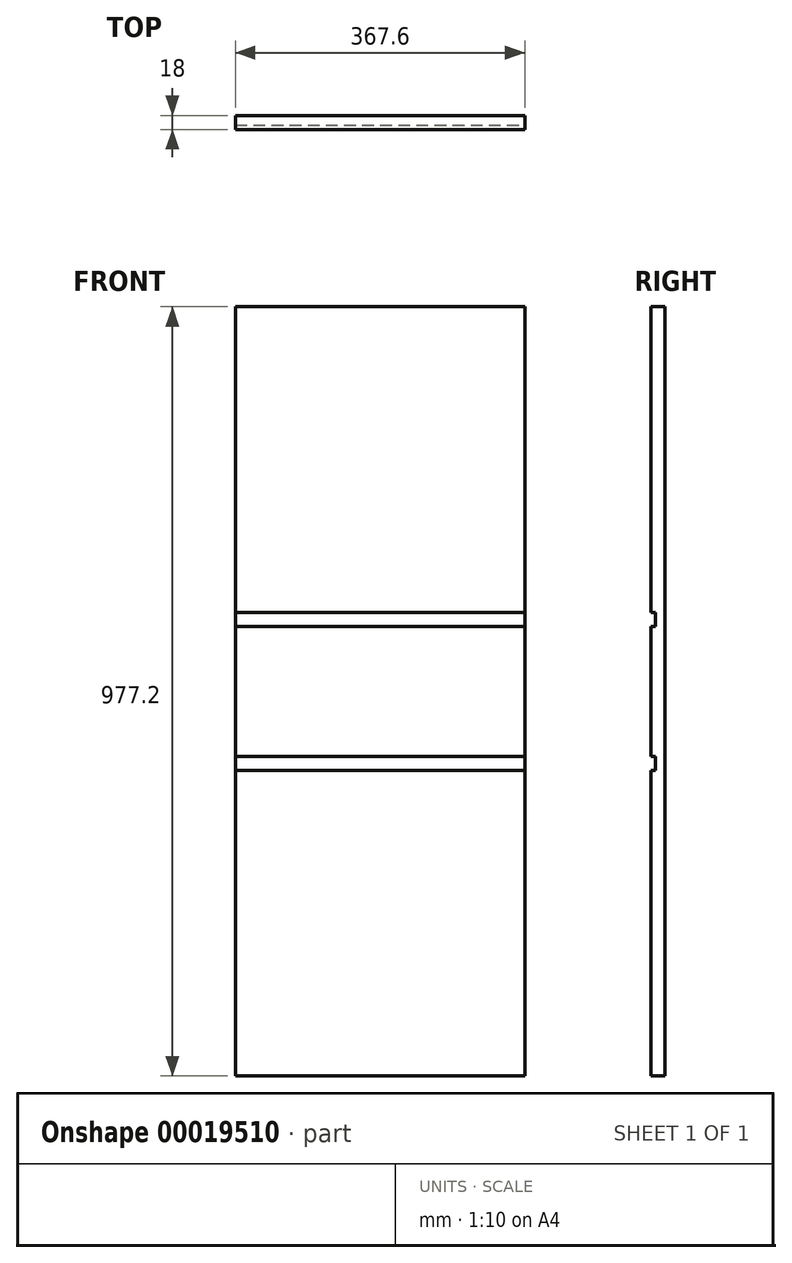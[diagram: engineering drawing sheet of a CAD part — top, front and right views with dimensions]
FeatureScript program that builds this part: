
annotation { "Feature Type Name" : "Feature", "Feature Type Description" : "" }
export const myFeature = defineFeature(function(context is Context, id is Id, definition is map)
    precondition{}
    {
        {
            var Q0;
            Q0=qCreatedBy(makeId("Front.planeOp"),FACE);
            var sketch = newSketch(context, id + "F0", { "sketchPlane" : qUnion([Q0])});
            skLineSegment(sketch, "E0.bottom", {"start": v(-210.04, 655.45) * mm, "end": v(157.56, 655.45) * mm});
            skLineSegment(sketch, "E0.top", {"start": v(-210.04, -321.75) * mm, "end": v(157.56, -321.75) * mm});
            skLineSegment(sketch, "E0.left", {"start": v(-210.04, 655.45) * mm, "end": v(-210.04, -321.75) * mm});
            skLineSegment(sketch, "E0.right", {"start": v(157.56, 655.45) * mm, "end": v(157.56, -321.75) * mm});
            skSolve(sketch);
        }
        {
            var Q0;
            Q0 = qSketchRegion(id + "F0", true);
            extrude(context, id + "F1", {"entities" : qUnion([Q0]), "depth" : 18 * mm});
        }
        {
            var Q0;
            Q0=makeQuery(id+"F1.opExtrude","CAP_FACE",FACE,{"disambiguationData":[OSD([sQuery(id+"F0.wireOp",EDGE,"E0.bottom"),sQuery(id+"F0.wireOp",EDGE,"E0.top"),sQuery(id+"F0.wireOp",EDGE,"E0.left"),sQuery(id+"F0.wireOp",EDGE,"E0.right")])],"isStart":false});
            var sketch = newSketch(context, id + "F2", { "sketchPlane" : qUnion([Q0])});
            skLineSegment(sketch, "E1", {"start": v(-210.04, 166.85) * mm, "end": v(157.56, 166.85) * mm, "construction": true});
            skLineSegment(sketch, "E2", {"start": v(-26.24, 655.45) * mm, "end": v(-26.24, -321.75) * mm, "construction": true});
            skLineSegment(sketch, "E3.bottom", {"start": v(-296.1, 267.4) * mm, "end": v(259, 267.4) * mm});
            skLineSegment(sketch, "E3.top", {"start": v(-296.1, 249.4) * mm, "end": v(259, 249.4) * mm});
            skLineSegment(sketch, "E3.left", {"start": v(-296.1, 267.4) * mm, "end": v(-296.1, 249.4) * mm});
            skLineSegment(sketch, "E3.right", {"start": v(259, 267.4) * mm, "end": v(259, 249.4) * mm});
            skLineSegment(sketch, "E4.bottom", {"start": v(-279.46, 84.3) * mm, "end": v(284.7, 84.3) * mm});
            skLineSegment(sketch, "E4.top", {"start": v(-279.46, 66.3) * mm, "end": v(284.7, 66.3) * mm});
            skLineSegment(sketch, "E4.left", {"start": v(-279.46, 84.3) * mm, "end": v(-279.46, 66.3) * mm});
            skLineSegment(sketch, "E4.right", {"start": v(284.7, 84.3) * mm, "end": v(284.7, 66.3) * mm});
            skSolve(sketch);
        }
        {
            var Q0;
            Q0 = qSketchRegion(id + "F2", true);
            extrude(context, id + "F3", {"entities" : qUnion([Q0]), "operationType" : NewBodyOperationType.REMOVE, "oppositeDirection" : true, "depth" : 6 * mm});
        }
    });
